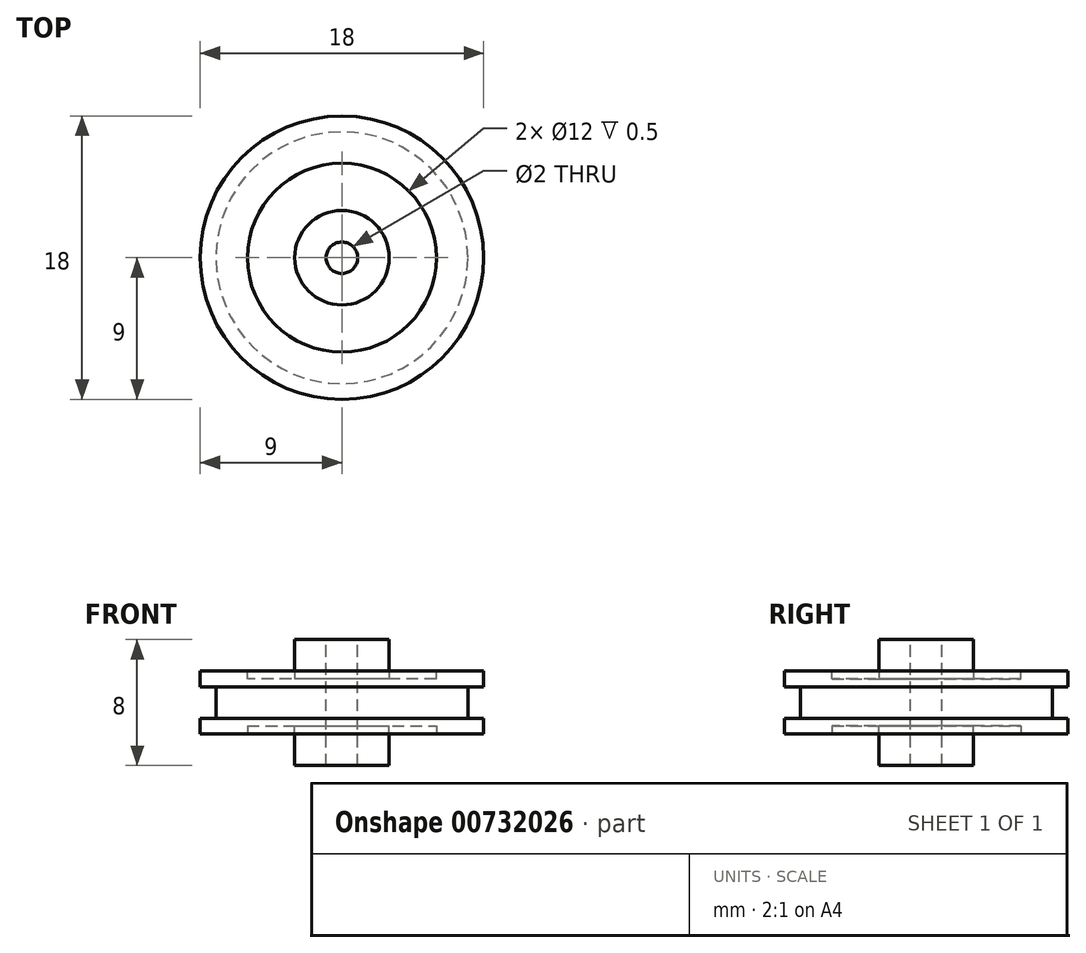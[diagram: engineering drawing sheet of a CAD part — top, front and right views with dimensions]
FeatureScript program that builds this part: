
annotation { "Feature Type Name" : "Feature", "Feature Type Description" : "" }
export const myFeature = defineFeature(function(context is Context, id is Id, definition is map)
    precondition{}
    {
        {
            var Q0;
            Q0=qCreatedBy(makeId("Top.planeOp"),FACE);
            var sketch = newSketch(context, id + "F0", { "sketchPlane" : qUnion([Q0])});
            skCircle(sketch, "E0", {"center": v(0, 0) * mm, "radius": 9 * mm});
            skSolve(sketch);
        }
        {
            var Q0;
            Q0 = qSketchRegion(id + "F0", true);
            var Q1;
            Q1=makeQuery(id+"F0.imprint","IMPRINT",FACE,{"disambiguationData":[TD([[makeQuery(id+"F0.imprint","IMPRINT",EDGE,{"derivedFrom":sQuery(id+"F0.wireOp",EDGE,"E0")}),1.0]])]});
            extrude(context, id + "F1", {"entities" : qUnion([Q0, Q1]), "depth" : 4 * mm, "offsetDistance" : 25 * mm});
        }
        {
            var Q0;
            Q0=makeQuery(id+"F1.opExtrude","CAP_FACE",FACE,{"disambiguationData":[OSD([sQuery(id+"F0.wireOp",EDGE,"E0")])],"isStart":false});
            var sketch = newSketch(context, id + "F2", { "sketchPlane" : qUnion([Q0])});
            skCircle(sketch, "E1", {"center": v(0, 0) * mm, "radius": 6 * mm});
            skSolve(sketch);
        }
        {
            var Q0;
            Q0=makeQuery(id+"F2.imprint","IMPRINT",FACE,{"disambiguationData":[TD([[makeQuery(id+"F2.imprint","IMPRINT",EDGE,{"derivedFrom":sQuery(id+"F2.wireOp",EDGE,"E1")}),1.0]])]});
            extrude(context, id + "F3", {"entities" : qUnion([Q0]), "operationType" : NewBodyOperationType.REMOVE, "oppositeDirection" : true, "depth" : .5 * mm, "offsetDistance" : 25 * mm});
        }
        {
            var Q0;
            Q0=makeQuery(id+"F1.opExtrude","CAP_FACE",FACE,{"disambiguationData":[OSD([sQuery(id+"F0.wireOp",EDGE,"E0")])],"isStart":true});
            var sketch = newSketch(context, id + "F4", { "sketchPlane" : qUnion([Q0])});
            skCircle(sketch, "E2", {"center": v(0, 0) * mm, "radius": 6 * mm});
            skSolve(sketch);
        }
        {
            var Q0;
            Q0=makeQuery(id+"F4.imprint","IMPRINT",FACE,{"disambiguationData":[TD([[makeQuery(id+"F4.imprint","IMPRINT",EDGE,{"derivedFrom":sQuery(id+"F4.wireOp",EDGE,"E2")}),1.0]])]});
            extrude(context, id + "F5", {"entities" : qUnion([Q0]), "operationType" : NewBodyOperationType.REMOVE, "oppositeDirection" : true, "depth" : .5 * mm, "offsetDistance" : 25 * mm});
        }
        {
            var Q0;
            Q0=makeQuery(id+"F3.boolean.opBoolean","COPY",FACE,{"derivedFrom":makeQuery(id+"F3.opExtrude","CAP_FACE",FACE,{"disambiguationData":[OSD([sQuery(id+"F2.wireOp",EDGE,"E1")])],"isStart":false})});
            var sketch = newSketch(context, id + "F6", { "sketchPlane" : qUnion([Q0])});
            skCircle(sketch, "E3", {"center": v(0, 0) * mm, "radius": 3 * mm});
            skSolve(sketch);
        }
        {
            var Q0;
            Q0=makeQuery(id+"F6.imprint","IMPRINT",FACE,{"disambiguationData":[TD([[makeQuery(id+"F6.imprint","IMPRINT",EDGE,{"derivedFrom":sQuery(id+"F6.wireOp",EDGE,"E3")}),1.0]])]});
            extrude(context, id + "F7", {"entities" : qUnion([Q0]), "operationType" : NewBodyOperationType.ADD, "depth" : 2.5 * mm, "offsetDistance" : 25 * mm});
        }
        {
            var Q0;
            Q0=makeQuery(id+"F5.boolean.opBoolean","COPY",FACE,{"derivedFrom":makeQuery(id+"F5.opExtrude","CAP_FACE",FACE,{"disambiguationData":[OSD([sQuery(id+"F4.wireOp",EDGE,"E2")])],"isStart":false})});
            var sketch = newSketch(context, id + "F8", { "sketchPlane" : qUnion([Q0])});
            skCircle(sketch, "E4", {"center": v(0, 0) * mm, "radius": 3 * mm});
            skSolve(sketch);
        }
        {
            var Q0;
            Q0 = qSketchRegion(id + "F8", true);
            extrude(context, id + "F9", {"entities" : qUnion([Q0]), "operationType" : NewBodyOperationType.ADD, "depth" : 2.5 * mm, "offsetDistance" : 25 * mm});
        }
        {
            var Q0;
            Q0=makeQuery(id+"F7.opExtrude","CAP_FACE",FACE,{"disambiguationData":[OSD([sQuery(id+"F6.wireOp",EDGE,"E3")])],"isStart":false});
            var sketch = newSketch(context, id + "F10", { "sketchPlane" : qUnion([Q0])});
            skCircle(sketch, "E5", {"center": v(0, 0) * mm, "radius": 1 * mm});
            skSolve(sketch);
        }
        {
            var Q0;
            Q0 = qSketchRegion(id + "F10", true);
            extrude(context, id + "F11", {"entities" : qUnion([Q0]), "operationType" : NewBodyOperationType.REMOVE, "oppositeDirection" : true, "depth" : 25 * mm, "offsetDistance" : 25 * mm});
        }
        {
            var Q0;
            Q0=qCreatedBy(makeId("Top.planeOp"),FACE);
            cPlane(context, id + "F12", {"entities" : qUnion([Q0]), "cplaneType" : CPlaneType.OFFSET, "offset" : 1 * mm, "width" : 150 * mm, "height" : 150 * mm});
        }
        {
            var Q0;
            Q0=qCreatedBy(id+"F12.planeOp",FACE);
            var sketch = newSketch(context, id + "F13", { "sketchPlane" : qUnion([Q0])});
            skCircle(sketch, "E6", {"center": v(0, 0) * mm, "radius": 8 * mm});
            skCircle(sketch, "E7", {"center": v(0, 0) * mm, "radius": 15.85 * mm});
            skSolve(sketch);
        }
        {
            var Q0;
            Q0 = qSketchRegion(id + "F13", true);
            extrude(context, id + "F14", {"entities" : qUnion([Q0]), "operationType" : NewBodyOperationType.REMOVE, "depth" : 2 * mm, "offsetDistance" : 25 * mm});
        }
    });
